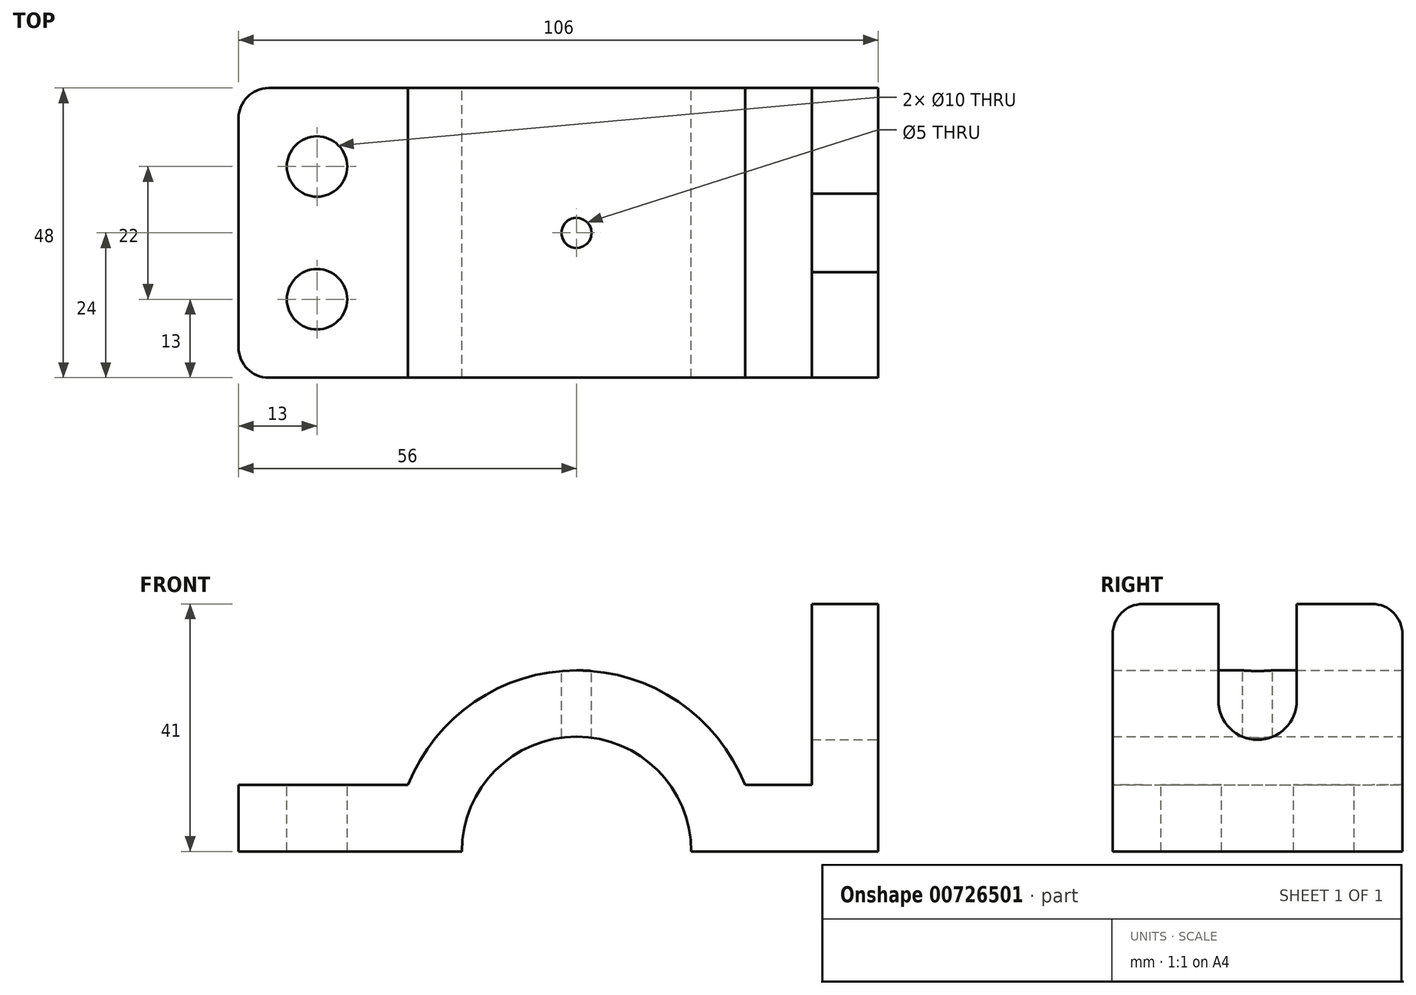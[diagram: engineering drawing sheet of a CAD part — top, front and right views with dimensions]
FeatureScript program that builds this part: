
annotation { "Feature Type Name" : "Feature", "Feature Type Description" : "" }
export const myFeature = defineFeature(function(context is Context, id is Id, definition is map)
    precondition{}
    {
        {
            var Q0;
            Q0=qCreatedBy(makeId("Front.planeOp"),FACE);
            var sketch = newSketch(context, id + "F0", { "sketchPlane" : qUnion([Q0])});
            skArc(sketch, "E0", {"start": v(19, 0) * mm, "mid": v(0, 19) * mm, "end": v(-19, 0) * mm});
            skLineSegment(sketch, "E1", {"start": v(50, 0) * mm, "end": v(50, 41) * mm});
            skLineSegment(sketch, "E2", {"start": v(50, 41) * mm, "end": v(39, 41) * mm});
            skLineSegment(sketch, "E3", {"start": v(39, 41) * mm, "end": v(39, 11) * mm});
            skArc(sketch, "E4", {"start": v(27.91, 11) * mm, "mid": v(0, 30) * mm, "end": v(-27.91, 11) * mm});
            skLineSegment(sketch, "E5", {"start": v(39, 11) * mm, "end": v(27.91, 11) * mm});
            skLineSegment(sketch, "E6", {"start": v(-56, 0) * mm, "end": v(-56, 11) * mm});
            skLineSegment(sketch, "E7", {"start": v(-56, 11) * mm, "end": v(-27.91, 11) * mm});
            skLineSegment(sketch, "E8.trimOffspring", {"start": v(-30, 0) * mm, "end": v(-56, 0) * mm});
            skLineSegment(sketch, "E9.trimOffspring", {"start": v(30, 0) * mm, "end": v(50, 0) * mm});
            skLineSegment(sketch, "E10", {"start": v(-30, 0) * mm, "end": v(-19, 0) * mm});
            skLineSegment(sketch, "E11", {"start": v(19, 0) * mm, "end": v(30, 0) * mm});
            skSolve(sketch);
        }
        {
            var Q0;
            Q0=makeQuery(id+"F0.imprint","IMPRINT",FACE,{"disambiguationData":[TD([[makeQuery(id+"F0.imprint","IMPRINT",EDGE,{"derivedFrom":sQuery(id+"F0.wireOp",EDGE,"E6")}),-1.0]])]});
            var Q1;
            Q1=makeQuery(id+"F0.imprint","IMPRINT",FACE,{"disambiguationData":[TD([[makeQuery(id+"F0.imprint","IMPRINT",EDGE,{"derivedFrom":sQuery(id+"F0.wireOp",EDGE,"E0")}),1.0]])]});
            var Q2;
            Q2=makeQuery(id+"F0.imprint","IMPRINT",FACE,{"disambiguationData":[TD([[makeQuery(id+"F0.imprint","IMPRINT",EDGE,{"derivedFrom":sQuery(id+"F0.wireOp",EDGE,"E0")}),-1.0]])]});
            extrude(context, id + "F1", {"entities" : qUnion([Q0, Q1, Q2]), "depth" : 48 * mm, "offsetDistance" : 25 * mm});
        }
        {
            var Q0;
            Q0=makeQuery(id+"F1.opExtrude","CAP_EDGE",EDGE,{"disambiguationData":[OSD([sQuery(id+"F0.wireOp",EDGE,"E2")])],"isStart":false});
            fillet(context, id + "F2", {"entities" : qUnion([Q0]), "radius" : 5 * mm, "tangentPropagation" : true, "allowEdgeOverflow" : false});
        }
        {
            var Q0;
            Q0=makeQuery(id+"F1.opExtrude","CAP_EDGE",EDGE,{"disambiguationData":[OSD([sQuery(id+"F0.wireOp",EDGE,"E2")])],"isStart":true});
            fillet(context, id + "F3", {"entities" : qUnion([Q0]), "radius" : 5 * mm, "tangentPropagation" : true, "allowEdgeOverflow" : false});
        }
        {
            var Q0;
            Q0=makeQuery(id+"F1.opExtrude","SWEPT_FACE",FACE,{"disambiguationData":[OSD([sQuery(id+"F0.wireOp",EDGE,"E1")])]});
            var sketch = newSketch(context, id + "F4", { "sketchPlane" : qUnion([Q0])});
            skLineSegment(sketch, "E12", {"start": v(0, 0) * mm, "end": v(0, 25) * mm});
            skArc(sketch, "E13", {"start": v(-30.5, 25) * mm, "mid": v(-24, 18.5) * mm, "end": v(-17.5, 25) * mm});
            skLineSegment(sketch, "E14", {"start": v(-30.5, 25) * mm, "end": v(-30.5, 41) * mm});
            skLineSegment(sketch, "E15", {"start": v(-17.5, 25) * mm, "end": v(-17.5, 41) * mm});
            skSolve(sketch);
        }
        {
            var Q0;
            Q0=makeQuery(id+"F4.imprint","IMPRINT",FACE,{"disambiguationData":[TD([[makeQuery(id+"F4.imprint","IMPRINT",EDGE,{"derivedFrom":sQuery(id+"F4.wireOp",EDGE,"E13")}),1.0]])]});
            extrude(context, id + "F5", {"entities" : qUnion([Q0]), "operationType" : NewBodyOperationType.REMOVE, "endBound" : BoundingType.UP_TO_NEXT, "oppositeDirection" : true, "depth" : 25 * mm, "offsetDistance" : 25 * mm});
        }
        {
            var Q0;
            Q0=makeQuery(id+"F1.opExtrude","CAP_EDGE",EDGE,{"disambiguationData":[OSD([sQuery(id+"F0.wireOp",EDGE,"E6")])],"isStart":false});
            fillet(context, id + "F6", {"entities" : qUnion([Q0]), "radius" : 5 * mm, "tangentPropagation" : true, "allowEdgeOverflow" : false});
        }
        {
            var Q0;
            Q0=makeQuery(id+"F1.opExtrude","CAP_EDGE",EDGE,{"disambiguationData":[OSD([sQuery(id+"F0.wireOp",EDGE,"E6")])],"isStart":true});
            fillet(context, id + "F7", {"entities" : qUnion([Q0]), "radius" : 5 * mm, "tangentPropagation" : true, "allowEdgeOverflow" : false});
        }
        {
            var Q0;
            Q0=makeQuery(id+"F1.opExtrude","SWEPT_FACE",FACE,{"disambiguationData":[OSD([sQuery(id+"F0.wireOp",EDGE,"E7")])]});
            var sketch = newSketch(context, id + "F8", { "sketchPlane" : qUnion([Q0])});
            skCircle(sketch, "E16", {"center": v(-43, -13) * mm, "radius": 5 * mm});
            skCircle(sketch, "E17", {"center": v(-43, -35) * mm, "radius": 5 * mm});
            skSolve(sketch);
        }
        {
            var Q0;
            Q0=makeQuery(id+"F8.imprint","IMPRINT",FACE,{"disambiguationData":[TD([[makeQuery(id+"F8.imprint","IMPRINT",EDGE,{"derivedFrom":sQuery(id+"F8.wireOp",EDGE,"E16")}),1.0]])]});
            var Q1;
            Q1=makeQuery(id+"F8.imprint","IMPRINT",FACE,{"disambiguationData":[TD([[makeQuery(id+"F8.imprint","IMPRINT",EDGE,{"derivedFrom":sQuery(id+"F8.wireOp",EDGE,"E17")}),1.0]])]});
            extrude(context, id + "F9", {"entities" : qUnion([Q0, Q1]), "operationType" : NewBodyOperationType.REMOVE, "endBound" : BoundingType.UP_TO_NEXT, "oppositeDirection" : true, "depth" : 25 * mm, "offsetDistance" : 25 * mm});
        }
        {
            var Q0;
            Q0=qCreatedBy(makeId("Top.planeOp"),FACE);
            cPlane(context, id + "F10", {"entities" : qUnion([Q0]), "cplaneType" : CPlaneType.OFFSET, "offset" : 30 * mm, "width" : 150 * mm, "height" : 150 * mm});
        }
        {
            var Q0;
            Q0=qCreatedBy(id+"F10.planeOp",FACE);
            var sketch = newSketch(context, id + "F11", { "sketchPlane" : qUnion([Q0])});
            skCircle(sketch, "E18", {"center": v(0, -24) * mm, "radius": 2.5 * mm});
            skSolve(sketch);
        }
        {
            var Q0;
            Q0 = qSketchRegion(id + "F11", true);
            extrude(context, id + "F12", {"entities" : qUnion([Q0]), "operationType" : NewBodyOperationType.REMOVE, "endBound" : BoundingType.UP_TO_NEXT, "oppositeDirection" : true, "depth" : 25 * mm, "offsetDistance" : 25 * mm});
        }
    });
